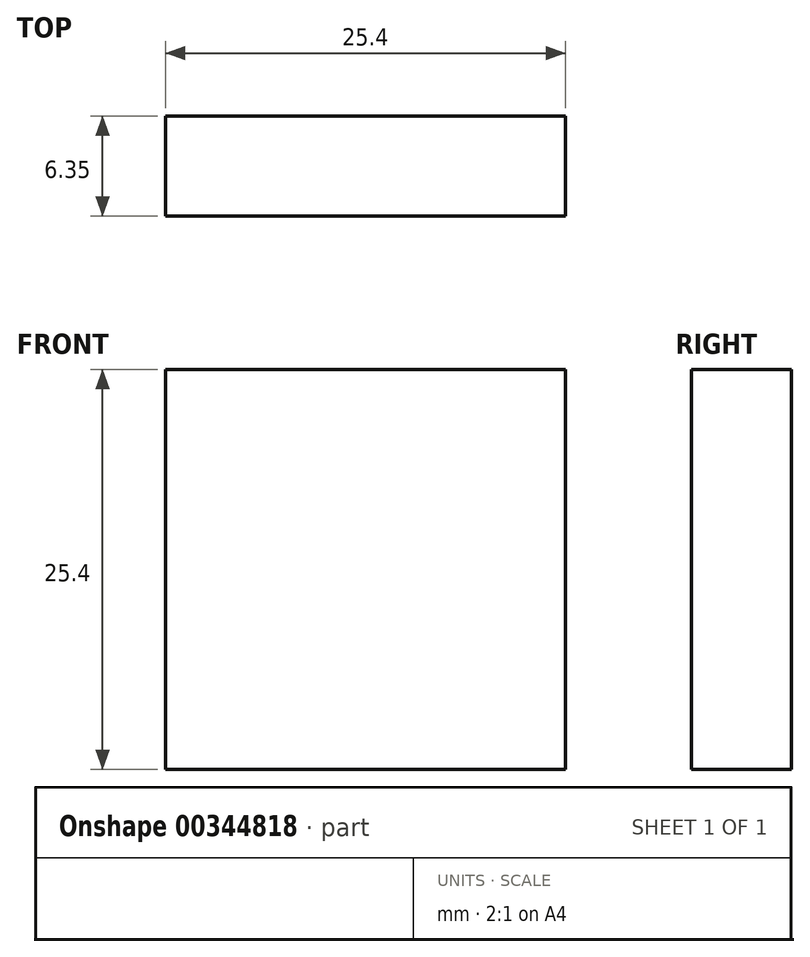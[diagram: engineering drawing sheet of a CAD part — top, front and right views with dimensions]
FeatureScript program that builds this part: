
annotation { "Feature Type Name" : "Feature", "Feature Type Description" : "" }
export const myFeature = defineFeature(function(context is Context, id is Id, definition is map)
    precondition{}
    {
        {
            var Q0;
            Q0=qCreatedBy(makeId("Front.planeOp"),FACE);
            var sketch = newSketch(context, id + "F0", { "sketchPlane" : qUnion([Q0])});
            skLineSegment(sketch, "E0.bottom", {"start": v(0, 0) * mm, "end": v(25.4, 0) * mm});
            skLineSegment(sketch, "E0.top", {"start": v(0, 25.4) * mm, "end": v(25.4, 25.4) * mm});
            skLineSegment(sketch, "E0.left", {"start": v(0, 0) * mm, "end": v(0, 25.4) * mm});
            skLineSegment(sketch, "E0.right", {"start": v(25.4, 0) * mm, "end": v(25.4, 25.4) * mm});
            skSolve(sketch);
        }
        {
            var Q0;
            Q0=makeQuery(id+"F0.imprint","IMPRINT",FACE,{"disambiguationData":[TD([[makeQuery(id+"F0.imprint","IMPRINT",EDGE,{"derivedFrom":sQuery(id+"F0.wireOp",EDGE,"E0.bottom")}),1.0]])]});
            extrude(context, id + "F1", {"entities" : qUnion([Q0]), "depth" : 6.35 * mm});
        }
    });
